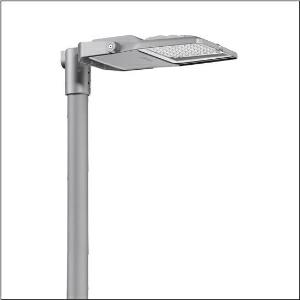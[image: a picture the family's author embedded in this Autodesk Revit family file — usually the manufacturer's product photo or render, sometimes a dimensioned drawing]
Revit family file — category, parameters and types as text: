
# Revit family: floodlight_fl_21_iq_mini___pl61_5xa7772b4c3a_beff
name_source: partatom
category: Lighting Fixtures
units: mm (PartAtom-declared; Revit-internal decimal feet)

## family parameters
Cut with Voids When Loaded = No
Host = Face
Light Source = No
Part Type = Normal
Room Calculation Point = No
Round Connector Dimension = Use Diameter
Shared = No

## types (1)
- --- (1 x LED, 6370 lm, 45.5 W, 4000K)
    Apparent Load = 46 VA
    CIE Flux Codes = 33 65 98 100 100
    Color Rendering = 70
    Color Temperature = 4000K
    Default Elevation = 1800 mm
    Description = Floodlight FL 21 iQ mini, floodlight, primary light control with lens, of PMMA, primary optical cover: protective disc, of toughened safety glass, transparent, light distribution: PL61, light emission: direct distribution, installation type: surface-mounted, LED, High Power LED, rated luminous flux: 6.370lm, luminous efficacy: 140lm/W, light colour: 740, colour temperature: 4000K, control: Auto-Match, Temp-Guard, Night-Set, Smart-Wire, Desk-Remote (wireless, voltage-free reading and setting of iQ features in the workshop via application-optimized NFC function/RFID function), optimised constant luminous flux control (CLO 2.0), Light-Fading, Lumen-Switch, with terminal, 6-pole, mains connection: 220..240V, AC, 50/60Hz, start of lifetime: 46W, end of service life: 48W, reduction: 22W, luminaire housing, of diecast aluminium, powder-coated, Siteco® metallic grey (DB 702S), corrosivity category C5 mid according to DIN EN ISO 12944, sealing non-destructively replaceable, please order mast flange separately, mast bracket, of steel, galvanised, powder-coated, protection rating (complete): IP66, insulation class (complete): insulation class II (safety insulation), certification: CE, ENEC, VDE, protection symbol: D, impact resistance: IK08, permissible operating ambient temperature: -40..+40°C, permissible operating ambient temperature for outdoor applications: -40..+50°C, standard: DIN EN 12944, LABS conformity tested according to VDMA 24364:2018-05, packaging unit: 1 piece

Light Distribution: PL61
    Height = 70 mm
    Lamp = 1 x LED
    Lamp Light Flux = 6370 lm
    Lamp Power = 45.5 W
    Lamp count = 1
    Length = 485 mm
    Luminous efficacy = 140 lm/W
    Manufacturer = Siteco
    ModVariant = No
    Model = 5XA7772B4C3A
    Number of Poles = 1
    OnlyDefault = Yes
    Power Factor = 1
    Product Name = Floodlight FL 21 iQ mini | PL61
    Product group = floodlight | pylon annexe
    ProductGroupID = 6200
    Protection Class = Protection class II
    Protection Degree = IP 66
    RLX_Detail_Level = 1
    RLX_Emergency_Light_Flux = 0 lm
    RLX_Emergency_Type = 0
    RLX_Emergency_Type_DB = No
    RlxData = <blob elided: 101269 chars, md5=716f305a>
    Socket = socket
    Standby Power = 0 W
    System Light Flux = 6370 lm
    System Power = 46 W
    Type Comments = factory setting: luminous flux: 100 % | dim-lin: 254 | 463 mA
    Type Image = l_1007125.jpg
    URL = http://relux.com
    VarID = @adj_144549
    Voltage = 0 V
    Weight = 0.00 kg
    Width = 337 mm

## geometry (parser evidence)
native form markers: Blend x4, Sweep x14
no freeform markers — native parametric forms only
